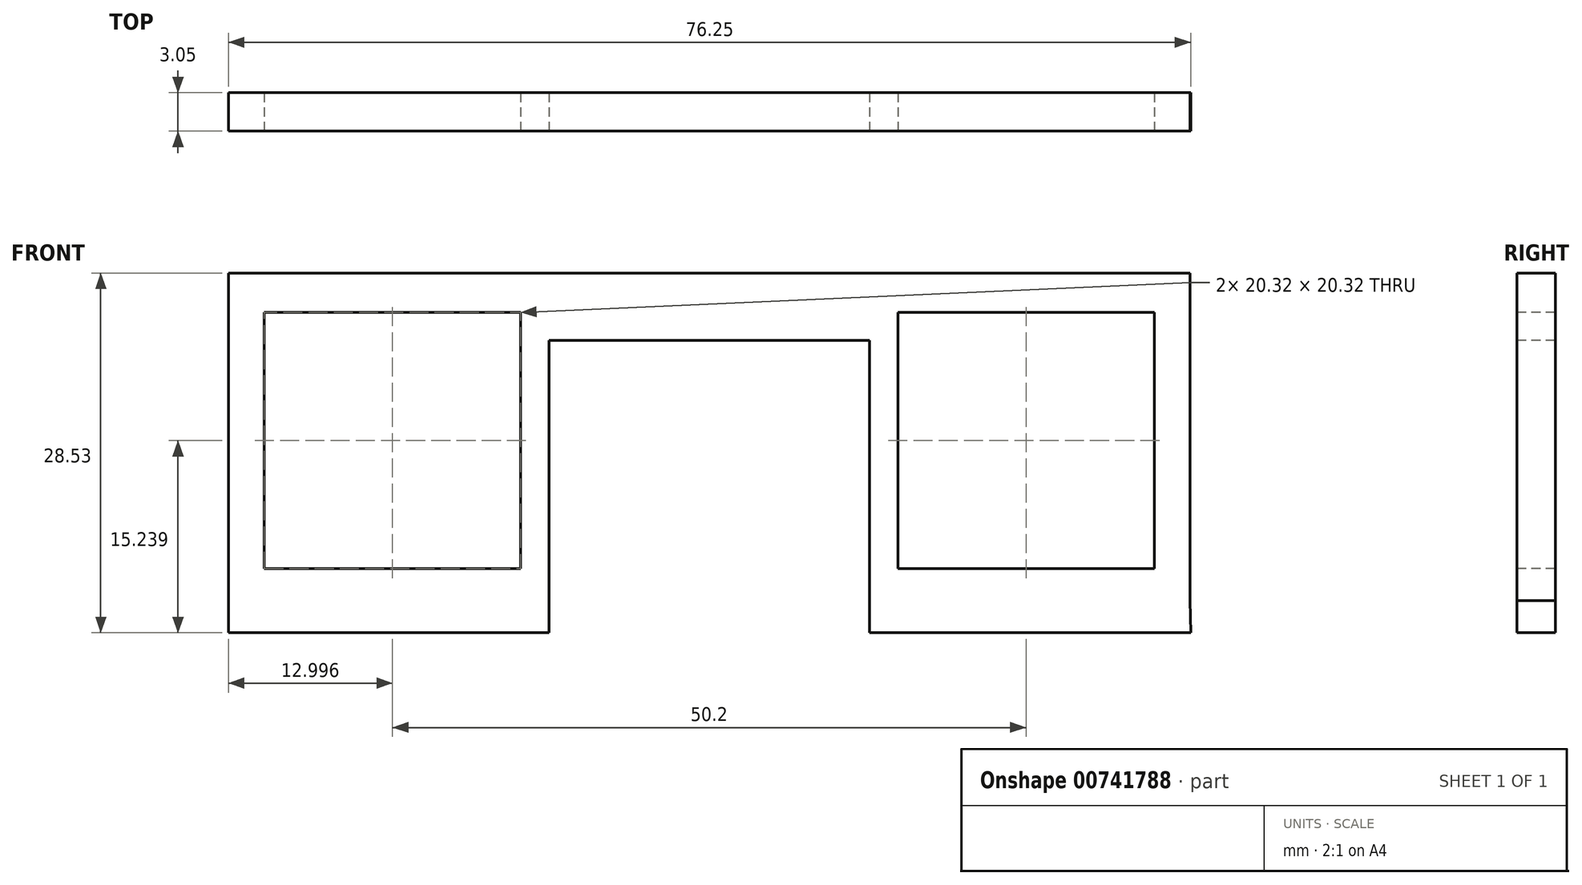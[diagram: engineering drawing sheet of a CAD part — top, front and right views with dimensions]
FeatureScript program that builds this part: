
annotation { "Feature Type Name" : "Feature", "Feature Type Description" : "" }
export const myFeature = defineFeature(function(context is Context, id is Id, definition is map)
    precondition{}
    {
        {
            var Q0;
            Q0=qCreatedBy(makeId("Front.planeOp"),FACE);
            var sketch = newSketch(context, id + "F0", { "sketchPlane" : qUnion([Q0])});
            skLineSegment(sketch, "E0.bottom", {"start": v(-37.94, 34.23) * mm, "end": v(-12.54, 34.23) * mm});
            skLineSegment(sketch, "E0.top", {"start": v(-37.94, 8.24) * mm, "end": v(-12.54, 8.24) * mm});
            skLineSegment(sketch, "E0.left", {"start": v(-37.94, 34.23) * mm, "end": v(-37.94, 8.24) * mm});
            skLineSegment(sketch, "E0.right", {"start": v(-12.54, 34.23) * mm, "end": v(-12.54, 8.24) * mm});
            skLineSegment(sketch, "E1.right", {"start": v(-12.54, 34.23) * mm, "end": v(-12.54, 33.18) * mm});
            skLineSegment(sketch, "E2.bottom", {"start": v(12.86, 34.23) * mm, "end": v(38.26, 34.23) * mm});
            skLineSegment(sketch, "E2.top", {"start": v(12.86, 8.24) * mm, "end": v(38.26, 8.24) * mm});
            skLineSegment(sketch, "E2.left", {"start": v(12.86, 34.23) * mm, "end": v(12.86, 8.24) * mm});
            skLineSegment(sketch, "E2.right", {"start": v(38.26, 34.23) * mm, "end": v(38.26, 8.24) * mm});
            skLineSegment(sketch, "E3", {"start": v(-12.54, 34.23) * mm, "end": v(12.86, 34.23) * mm});
            skLineSegment(sketch, "E4", {"start": v(-12.54, 28.88) * mm, "end": v(12.86, 28.88) * mm});
            skLineSegment(sketch, "E5.bottom", {"start": v(-35.1, 31.1) * mm, "end": v(-14.78, 31.1) * mm});
            skLineSegment(sketch, "E5.top", {"start": v(-35.1, 10.78) * mm, "end": v(-14.78, 10.78) * mm});
            skLineSegment(sketch, "E5.left", {"start": v(-35.1, 31.1) * mm, "end": v(-35.1, 10.78) * mm});
            skLineSegment(sketch, "E5.right", {"start": v(-14.78, 31.1) * mm, "end": v(-14.78, 10.78) * mm});
            skLineSegment(sketch, "E6.bottom", {"start": v(15.1, 31.1) * mm, "end": v(35.42, 31.1) * mm});
            skLineSegment(sketch, "E6.top", {"start": v(15.1, 10.78) * mm, "end": v(35.42, 10.78) * mm});
            skLineSegment(sketch, "E6.left", {"start": v(15.1, 31.1) * mm, "end": v(15.1, 10.78) * mm});
            skLineSegment(sketch, "E6.right", {"start": v(35.42, 31.1) * mm, "end": v(35.42, 10.78) * mm});
            skLineSegment(sketch, "E7", {"start": v(-37.94, 8.24) * mm, "end": v(-37.94, 5.7) * mm});
            skLineSegment(sketch, "E8", {"start": v(-37.94, 5.7) * mm, "end": v(-12.53, 5.7) * mm});
            skLineSegment(sketch, "E9", {"start": v(-12.53, 5.7) * mm, "end": v(-12.54, 8.24) * mm});
            skLineSegment(sketch, "E10", {"start": v(12.86, 8.24) * mm, "end": v(12.86, 5.7) * mm});
            skLineSegment(sketch, "E11", {"start": v(12.86, 5.7) * mm, "end": v(38.31, 5.7) * mm});
            skLineSegment(sketch, "E12", {"start": v(38.31, 5.7) * mm, "end": v(38.26, 8.24) * mm});
            skSolve(sketch);
        }
        {
            var Q0;
            Q0 = qSketchRegion(id + "F0", true);
            extrude(context, id + "F1", {"entities" : qUnion([Q0]), "oppositeDirection" : true, "depth" : 3.05 * mm, "offsetDistance" : 25.4 * mm});
        }
    });
